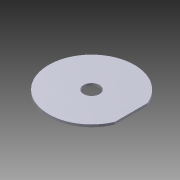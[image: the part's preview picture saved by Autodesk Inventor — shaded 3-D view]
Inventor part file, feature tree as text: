
AUTODESK INVENTOR PART (.ipt)
format: ipt  version: 2015 (Build 190159000, 159)  size: 83,456 bytes
history: native  units: mm
features: extrude x1, sketch x1
ambient origin geometry x8: Origin, YZ Plane, XZ Plane, XY Plane, X Axis, Y Axis, Z Axis, Center Point
bodies: Body1 (feature_tree)
feature tree (2):
  extrude  "Extrusion3"  Depth=3.0mm
  sketch  "Sketch1"  dims[d0=108.0mm d1=20.0mm d12=50.0mm d14=54.0mm d17=3.0mm d18=0.0mm]
